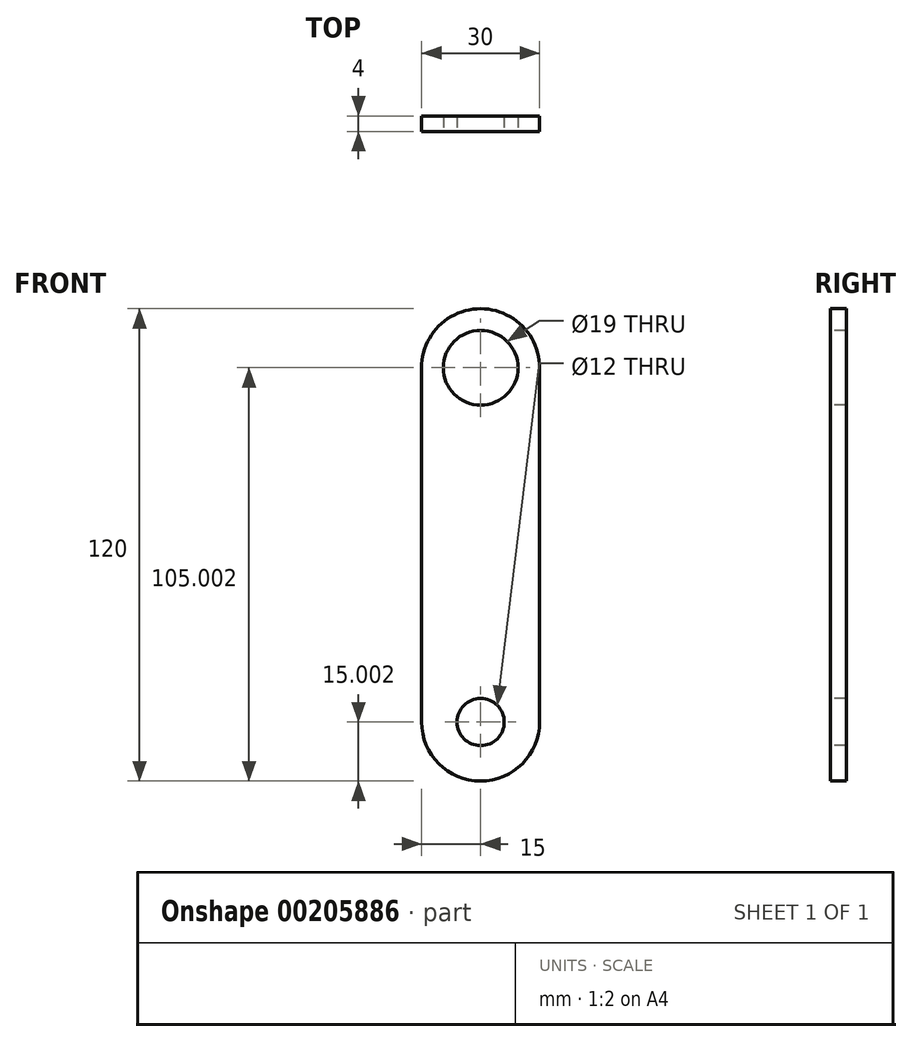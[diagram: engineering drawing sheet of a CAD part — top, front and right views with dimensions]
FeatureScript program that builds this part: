
annotation { "Feature Type Name" : "Feature", "Feature Type Description" : "" }
export const myFeature = defineFeature(function(context is Context, id is Id, definition is map)
    precondition{}
    {
        {
            var Q0;
            Q0=qCreatedBy(makeId("Front.planeOp"),FACE);
            var sketch = newSketch(context, id + "F0", { "sketchPlane" : qUnion([Q0])});
            skLineSegment(sketch, "E0.top", {"start": v(15, -53.84) * mm, "end": v(12.5, -53.84) * mm});
            skLineSegment(sketch, "E0.left", {"start": v(15, 36.16) * mm, "end": v(15, -53.84) * mm});
            skLineSegment(sketch, "E0.right", {"start": v(-15, 36.1) * mm, "end": v(-15, -53.84) * mm});
            skArc(sketch, "E1", {"start": v(15, 36.1) * mm, "mid": v(0, 51.16) * mm, "end": v(-15, 36.1) * mm});
            skArc(sketch, "E2", {"start": v(-15, -53.84) * mm, "mid": v(0, -68.84) * mm, "end": v(15, -53.84) * mm});
            skSolve(sketch);
        }
        {
            var Q0;
            Q0=qSketchRegion(id+"F0",true);
            extrude(context, id + "F1", {"entities" : qUnion([Q0]), "depth" : 4 * mm});
        }
        {
            var Q0;
            Q0=makeQuery(id+"F1.opExtrude","CAP_FACE",FACE,{"disambiguationData":[OSD([sQuery(id+"F0.wireOp",EDGE,"AU7xuiXe-0cF2-70zz-kpJU-1P1h8kQeCWXU"),sQuery(id+"F0.wireOp",EDGE,"ZtRF5qTW-I2TE-sx9C-qOHY-JpyusUdDcmJm"),sQuery(id+"F0.wireOp",EDGE,"E0.top"),sQuery(id+"F0.wireOp",EDGE,"E0.left"),sQuery(id+"F0.wireOp",EDGE,"E0.right")])],"isStart":false});
            var sketch = newSketch(context, id + "F2", { "sketchPlane" : qUnion([Q0])});
            skPoint(sketch, "E3", {"position": v(-7, 6.16) * mm});
            skPoint(sketch, "E4", {"position": v(7, 6.16) * mm});
            skPoint(sketch, "E5", {"position": v(7, -3.84) * mm});
            skPoint(sketch, "E6", {"position": v(-7, -3.84) * mm});
            skPoint(sketch, "E7", {"position": v(0, 36.16) * mm});
            skPoint(sketch, "E8", {"position": v(0, -53.84) * mm});
            skSolve(sketch);
        }
        {
            var Q0;
            Q0=sQuery(id+"F2.wireOp",VERTEX,"E7");
            var Q1;
            Q1=makeQuery(id+"F1.opExtrude","SWEPT_BODY",BODY,{"disambiguationData":[OSD([sQuery(id+"F0.wireOp",EDGE,"E0.left"),sQuery(id+"F0.wireOp",EDGE,"E0.right"),sQuery(id+"F0.wireOp",EDGE,"E1"),sQuery(id+"F0.wireOp",EDGE,"E2")])]});
            hole(context, id + "F3", {"style" : HoleStyle.SIMPLE, "endStyle" : HoleEndStyle.THROUGH, "holeDiameter" : 19 * mm, "locations" : qUnion([Q0]), "scope" : qUnion([Q1]), "isTappedThrough" : true});
        }
        {
            var Q0;
            Q0=sQuery(id+"F2.wireOp",VERTEX,"E8");
            var Q1;
            Q1=makeQuery(id+"F1.opExtrude","SWEPT_BODY",BODY,{"disambiguationData":[OSD([sQuery(id+"F0.wireOp",EDGE,"E0.left"),sQuery(id+"F0.wireOp",EDGE,"E0.right"),sQuery(id+"F0.wireOp",EDGE,"E1"),sQuery(id+"F0.wireOp",EDGE,"E2")])]});
            hole(context, id + "F4", {"style" : HoleStyle.SIMPLE, "endStyle" : HoleEndStyle.THROUGH, "holeDiameter" : 12 * mm, "locations" : qUnion([Q0]), "scope" : qUnion([Q1]), "isTappedThrough" : true});
        }
    });
